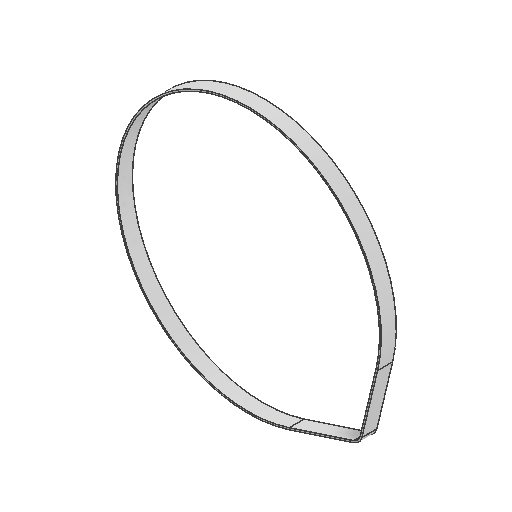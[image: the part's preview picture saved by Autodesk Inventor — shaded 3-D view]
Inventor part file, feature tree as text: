
AUTODESK INVENTOR PART (.ipt)
format: ipt  version: 2025.2 (Build 292293000, 293)  size: 110,080 bytes
history: native  units: in
note: dims shown in document units (in); Inventor stores cm internally (conversion verified against a paired STEP export)
features: extrude x1, sketch x1
ambient origin geometry x8: Origin, YZ Plane, XZ Plane, XY Plane, X Axis, Y Axis, Z Axis, Center Point
bodies: Solid1 (feature_tree)
feature tree (2):
  extrude  "Extrusion1"  Depth=0.358in
  sketch  "Sketch1"  dims[d0=6.2323in d1=0.4724in d2=3.3in d3=6.3123in d4=0.5524in d5=0.04in d6=0.04in d7=0.358in d8=0.0in]
